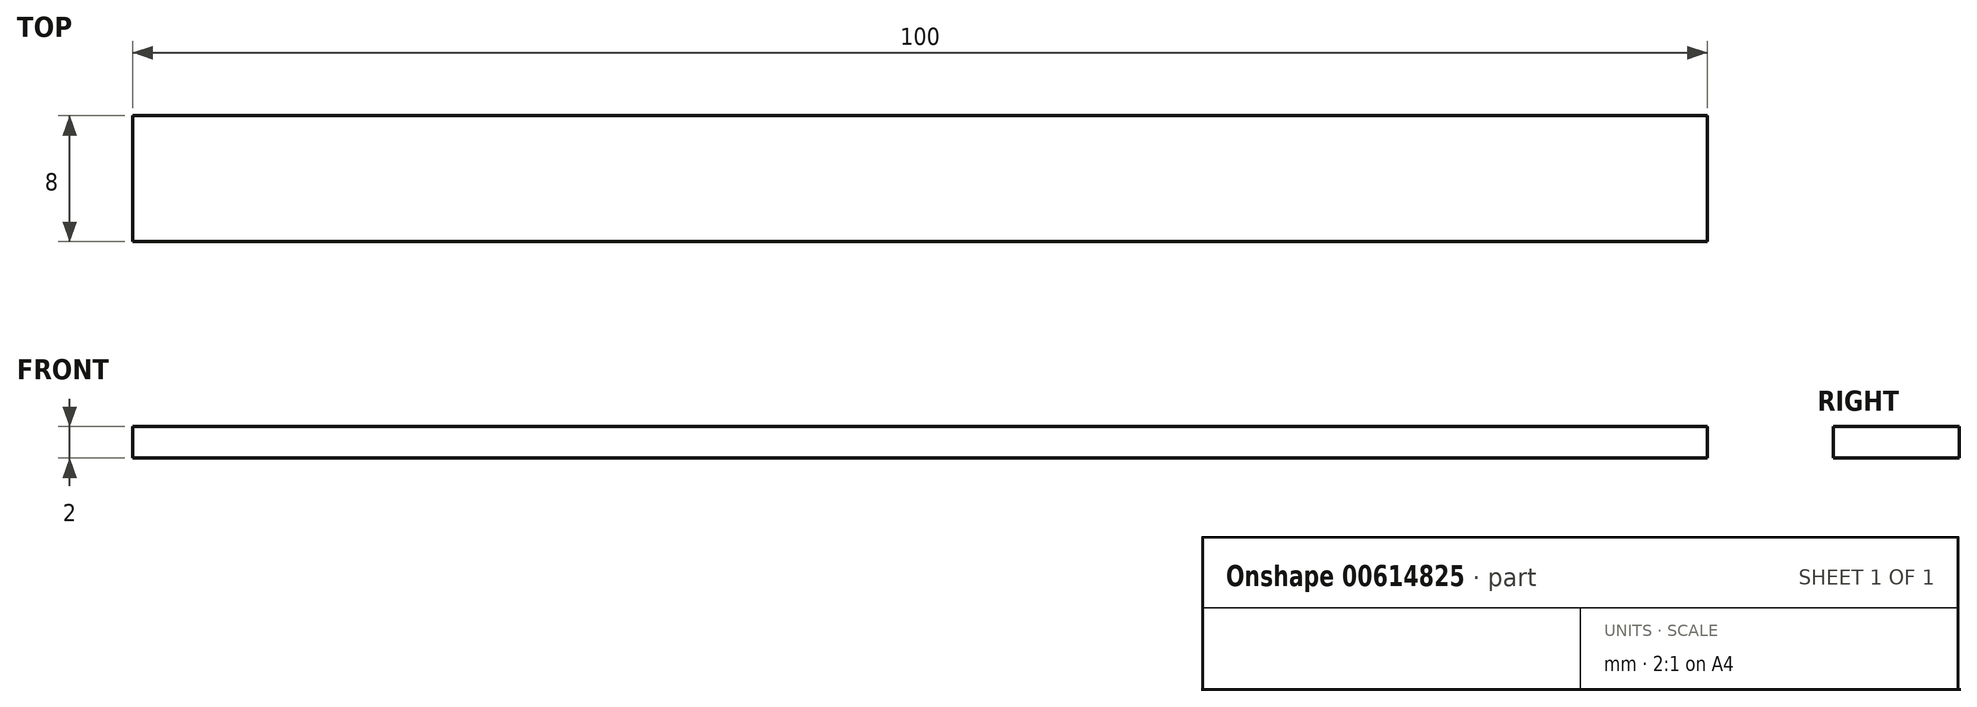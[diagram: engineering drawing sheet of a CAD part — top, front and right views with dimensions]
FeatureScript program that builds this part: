
annotation { "Feature Type Name" : "Feature", "Feature Type Description" : "" }
export const myFeature = defineFeature(function(context is Context, id is Id, definition is map)
    precondition{}
    {
        {
            var Q0;
            Q0=qCreatedBy(makeId("Top.planeOp"),FACE);
            var sketch = newSketch(context, id + "F0", { "sketchPlane" : qUnion([Q0])});
            skLineSegment(sketch, "E0.bottom", {"start": v(-58.44, 8) * mm, "end": v(41.56, 8) * mm});
            skLineSegment(sketch, "E0.top", {"start": v(-58.44, 0) * mm, "end": v(41.56, 0) * mm});
            skLineSegment(sketch, "E0.left", {"start": v(-58.44, 8) * mm, "end": v(-58.44, 0) * mm});
            skLineSegment(sketch, "E0.right", {"start": v(41.56, 8) * mm, "end": v(41.56, 0) * mm});
            skSolve(sketch);
        }
        {
            var Q0;
            Q0=makeQuery(id+"F0.imprint","IMPRINT",FACE,{"disambiguationData":[TD([[makeQuery(id+"F0.imprint","IMPRINT",EDGE,{"derivedFrom":sQuery(id+"F0.wireOp",EDGE,"E0.bottom")}),-1.0]])]});
            extrude(context, id + "F1", {"entities" : qUnion([Q0]), "depth" : 2 * mm, "offsetDistance" : 25 * mm});
        }
    });
